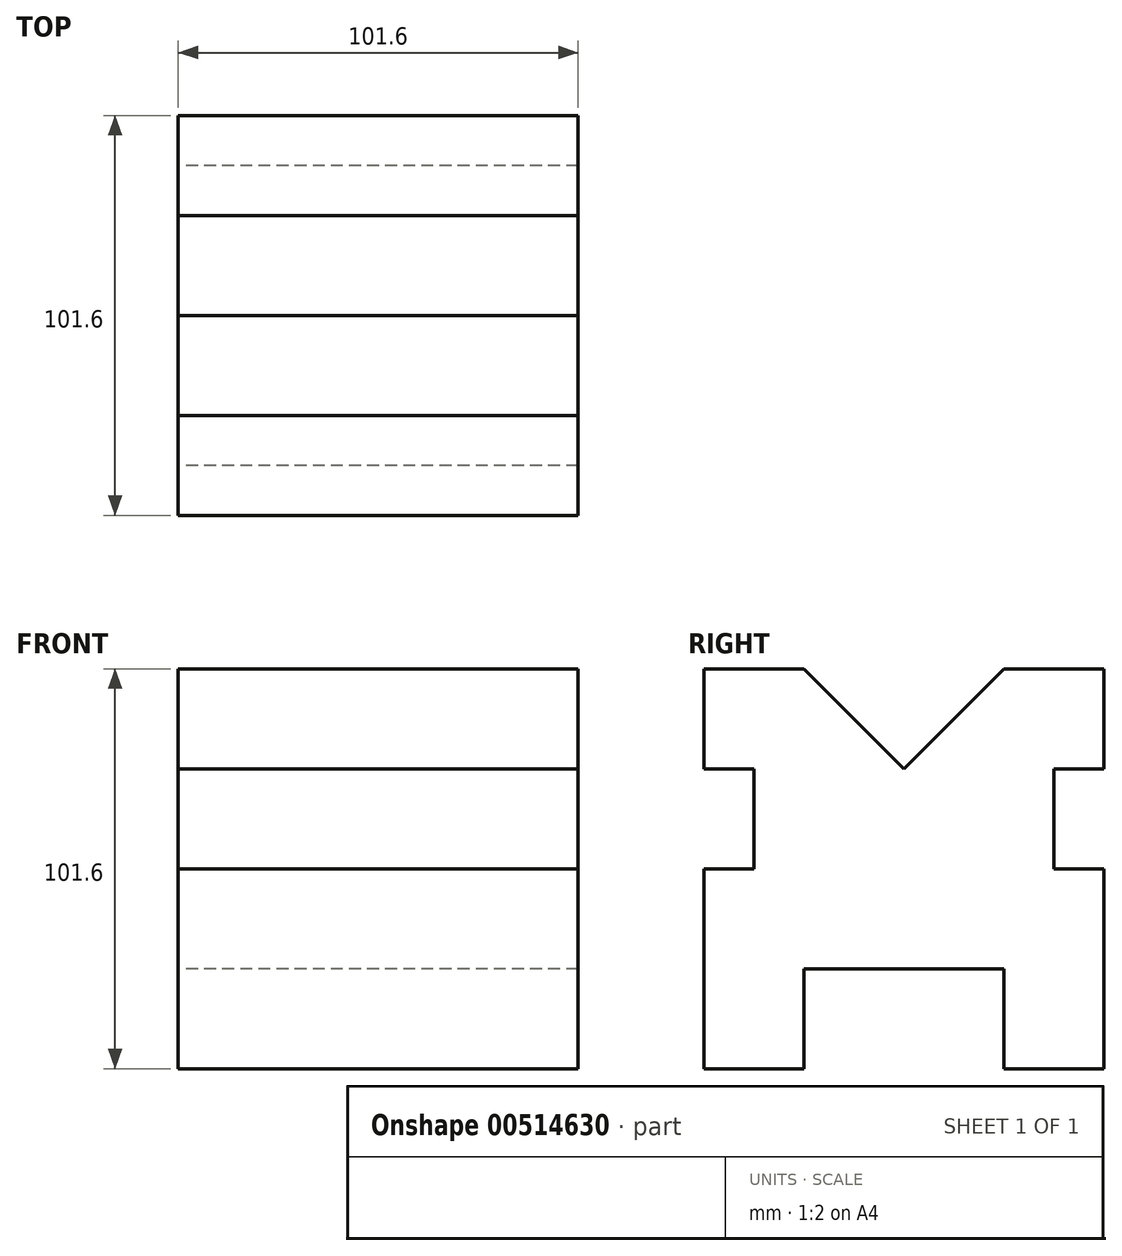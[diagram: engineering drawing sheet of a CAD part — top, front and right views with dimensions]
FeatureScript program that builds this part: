
annotation { "Feature Type Name" : "Feature", "Feature Type Description" : "" }
export const myFeature = defineFeature(function(context is Context, id is Id, definition is map)
    precondition{}
    {
        {
            var Q0;
            Q0=qCreatedBy(makeId("Right.planeOp"),FACE);
            var sketch = newSketch(context, id + "F0", { "sketchPlane" : qUnion([Q0])});
            skLineSegment(sketch, "E0", {"start": v(-75.95, -76.2) * mm, "end": v(-50.55, -76.2) * mm});
            skLineSegment(sketch, "E1", {"start": v(-50.55, -76.2) * mm, "end": v(-50.55, -50.8) * mm});
            skLineSegment(sketch, "E2", {"start": v(-50.55, -50.8) * mm, "end": v(0.25, -50.8) * mm});
            skLineSegment(sketch, "E3", {"start": v(0.25, -50.8) * mm, "end": v(0.25, -76.2) * mm});
            skLineSegment(sketch, "E4", {"start": v(0.25, -76.2) * mm, "end": v(25.65, -76.2) * mm});
            skLineSegment(sketch, "E5", {"start": v(25.65, -76.2) * mm, "end": v(25.65, -25.4) * mm});
            skLineSegment(sketch, "E6", {"start": v(-75.95, -76.2) * mm, "end": v(-75.95, -25.4) * mm});
            skLineSegment(sketch, "E7", {"start": v(-75.95, -25.4) * mm, "end": v(-63.25, -25.4) * mm});
            skLineSegment(sketch, "E8", {"start": v(25.65, -25.4) * mm, "end": v(12.95, -25.4) * mm});
            skLineSegment(sketch, "E9", {"start": v(-63.25, -25.4) * mm, "end": v(-63.25, 0) * mm});
            skLineSegment(sketch, "E10", {"start": v(12.95, -25.4) * mm, "end": v(12.95, 0) * mm});
            skLineSegment(sketch, "E11", {"start": v(-63.25, 0) * mm, "end": v(-75.95, 0) * mm});
            skLineSegment(sketch, "E12", {"start": v(12.95, 0) * mm, "end": v(25.65, 0) * mm});
            skLineSegment(sketch, "E13", {"start": v(-75.95, 0) * mm, "end": v(-75.95, 25.4) * mm});
            skLineSegment(sketch, "E14", {"start": v(25.65, 0) * mm, "end": v(25.65, 25.4) * mm});
            skLineSegment(sketch, "E15", {"start": v(-75.95, 25.4) * mm, "end": v(-50.55, 25.4) * mm});
            skLineSegment(sketch, "E16", {"start": v(25.65, 25.4) * mm, "end": v(0.25, 25.4) * mm});
            skLineSegment(sketch, "E17", {"start": v(-50.55, 25.4) * mm, "end": v(-25.15, 0) * mm});
            skPoint(sketch, "E17.endSnap0", {"position": v(-25.15, -50.8) * mm});
            skLineSegment(sketch, "E18", {"start": v(0.25, 25.4) * mm, "end": v(-25.15, 0) * mm});
            skSolve(sketch);
        }
        {
            var Q0;
            Q0=makeQuery(id+"F0.imprint","IMPRINT",FACE,{"disambiguationData":[TD([[makeQuery(id+"F0.imprint","IMPRINT",EDGE,{"derivedFrom":sQuery(id+"F0.wireOp",EDGE,"E0")}),1.0]])]});
            extrude(context, id + "F1", {"entities" : qUnion([Q0]), "depth" : 101.6 * mm, "offsetDistance" : 25.4 * mm});
        }
    });
